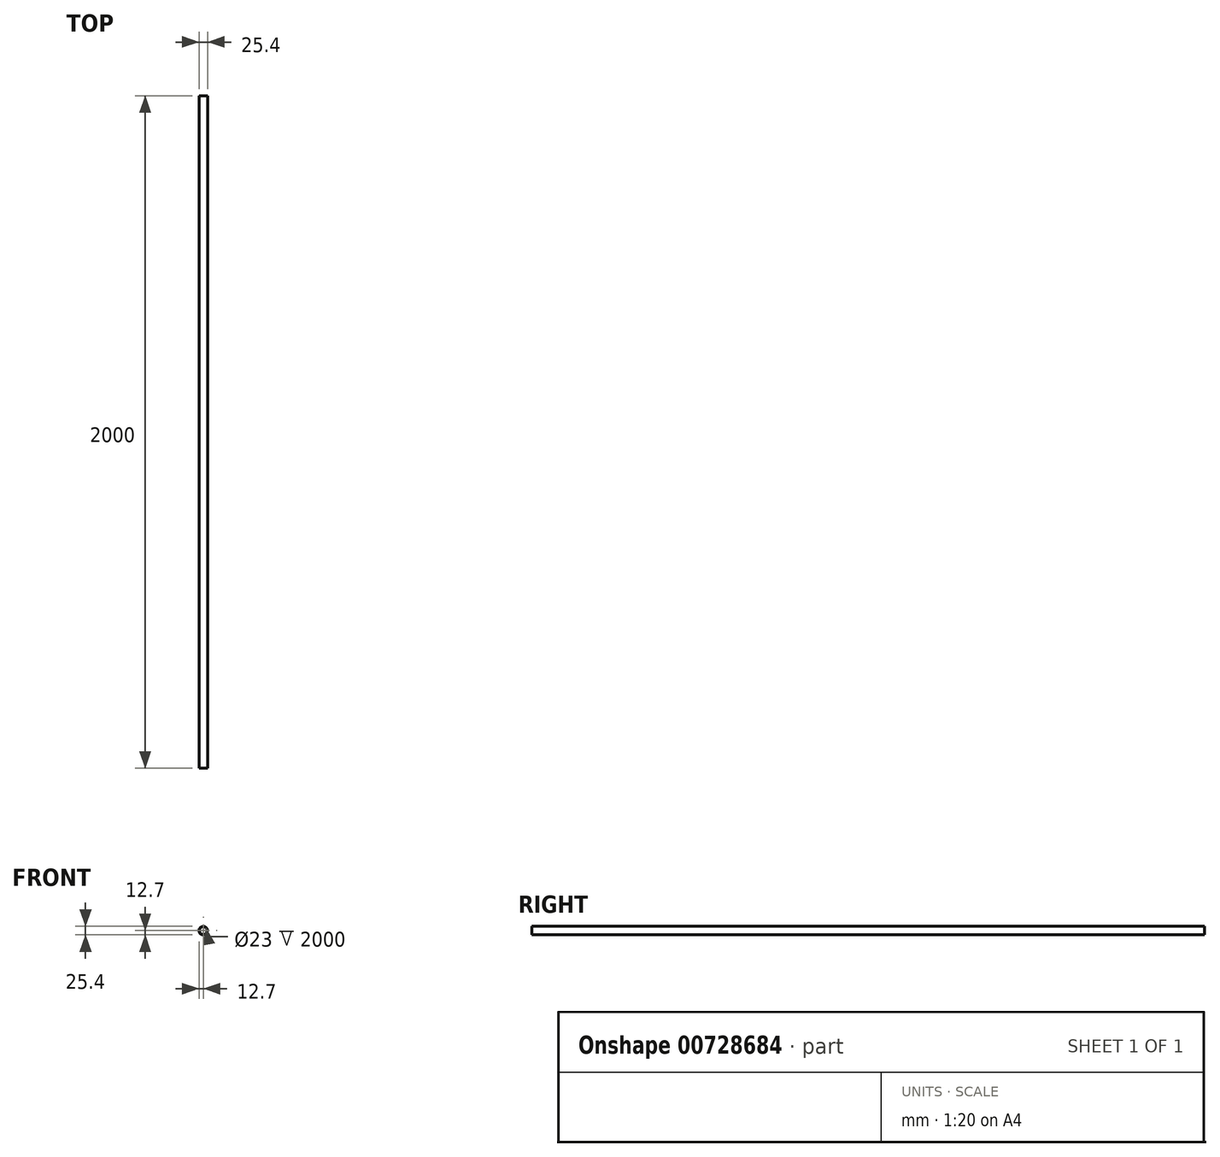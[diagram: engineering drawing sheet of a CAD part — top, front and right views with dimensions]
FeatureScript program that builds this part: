
annotation { "Feature Type Name" : "Feature", "Feature Type Description" : "" }
export const myFeature = defineFeature(function(context is Context, id is Id, definition is map)
    precondition{}
    {
        {
            var Q0;
            Q0=qCreatedBy(makeId("Front.planeOp"),FACE);
            var sketch = newSketch(context, id + "F0", { "sketchPlane" : qUnion([Q0])});
            skCircle(sketch, "E0", {"center": v(0, 0) * mm, "radius": 12.7 * mm});
            skCircle(sketch, "E1", {"center": v(0, 0) * mm, "radius": 11.5 * mm});
            skSolve(sketch);
        }
        {
            var Q0;
            Q0 = qSketchRegion(id + "F0", true);
            extrude(context, id + "F1", {"entities" : qUnion([Q0]), "endBound" : BoundingType.SYMMETRIC, "depth" : 2000 * mm, "offsetDistance" : 25 * mm});
        }
    });
